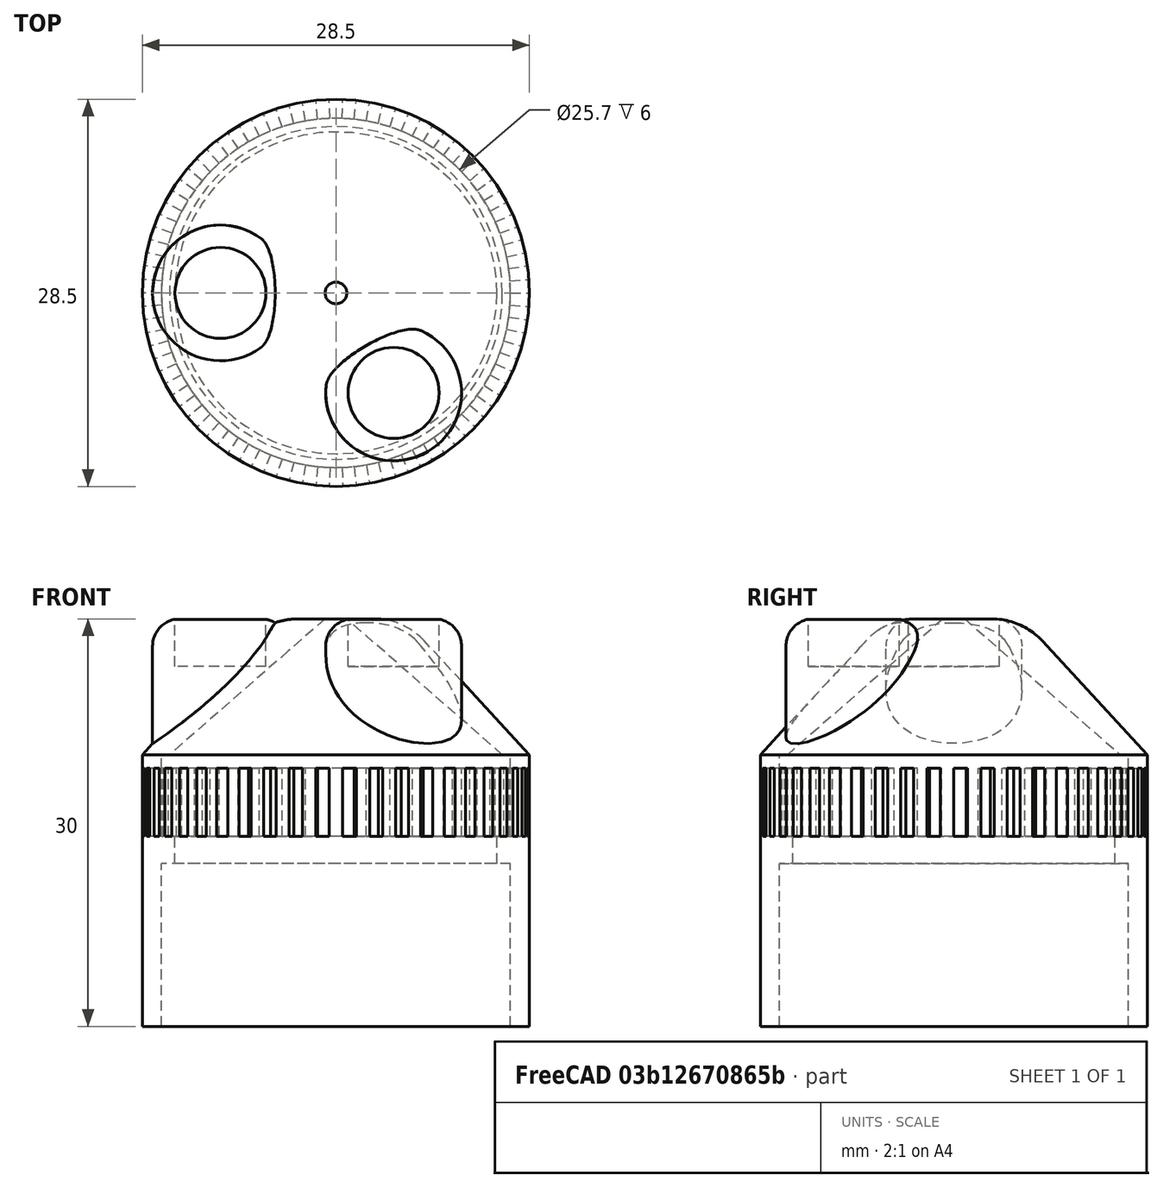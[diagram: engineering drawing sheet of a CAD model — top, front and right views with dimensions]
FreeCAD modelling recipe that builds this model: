
FCSTD DOCUMENT  (FreeCAD 0.17R11232 (Git))
Label: slotted_vial_to_funnel_adapter
License: All rights reserved
LicenseURL: http://en.wikipedia.org/wiki/All_rights_reserved
objects: Part::Feature×43, Part::Cylinder×9, Part::Cut×8, Part::MultiFuse×4, Part::Cone×3, Part::Fillet×3, Part::Box×1
note: 71 computed .brp shape members not serialized (recipe doc carries the construction recipe); baked Part::Feature solids carry a one-line shape summary decoded from their .brp

FEATURE [Part::Cylinder] Cylinder  label="outer_vial_sleeve_edge"
  Angle = 360
  AttacherType = Attacher::AttachEngine3D
  Height = 35
  Radius = 14.25
FEATURE [Part::Cylinder] Cylinder001  label="inner_vial_sleeve_edge"
  Angle = 360
  AttacherType = Attacher::AttachEngine3D
  Height = 35
  Radius = 12.85
FEATURE [Part::Cut] Cut  label="vial_sleeve"
  Base = -> Cylinder
  Tool = -> Cylinder001
FEATURE [Part::Cone] Cone  label="outer_ascent_cone_edge"
  Angle = 360
  AttacherType = Attacher::AttachEngine3D
  Height = 10
  Radius1 = 14.25
  Radius2 = 5
FEATURE [Part::Cone] Cone001  label="inner_ascent_cone_edge"
  Angle = 360
  AttacherType = Attacher::AttachEngine3D
  Height = 10
  Radius1 = 12.25
  Radius2 = 0.8
FEATURE [Part::Cut] Cut001  label="ascent_cone"
  Base = -> Cone
  Placement = pos=(0,0,35) rot=(0,0,1;0rad)
  Tool = -> Cone001
FEATURE [Part::Cylinder] Cylinder002  label="slot"
  Angle = 4
  AttacherType = Attacher::AttachEngine3D
  Height = 5
  Placement = pos=(0,0,29) rot=(0,0,1;0rad)
  Radius = 15
FEATURE [Part::Cylinder] Cylinder003  label="slot001"
  Angle = 4
  AttacherType = Attacher::AttachEngine3D
  Height = 5
  Placement = pos=(0,0,29) rot=(0,0,1;0.139626rad)
  Radius = 15
FEATURE [Part::Feature] Cylinder003002  label="slot003"
  Placement = pos=(0,0,29) rot=(0,0,1;0.279253rad)
  shape: bbox 14.42 x 5.13 x 5 mm, 5 faces (baked)
FEATURE [Part::Feature] slot_3  label="slot004"
  Placement = pos=(0,0,29) rot=(0,0,1;0.418879rad)
  shape: bbox 13.7 x 7.042 x 5 mm, 5 faces (baked)
FEATURE [Part::Feature] slot_4  label="slot005"
  Placement = pos=(0,0,29) rot=(0,0,1;0.558505rad)
  shape: bbox 12.72 x 8.817 x 5 mm, 5 faces (baked)
FEATURE [Part::Feature] slot_5  label="slot006"
  Placement = pos=(0,0,29) rot=(0,0,1;0.698132rad)
  shape: bbox 11.49 x 10.42 x 5 mm, 5 faces (baked)
FEATURE [Part::Feature] slot_6  label="slot007"
  Placement = pos=(0,0,29) rot=(0,0,1;0.837758rad)
  shape: bbox 10.04 x 11.82 x 5 mm, 5 faces (baked)
FEATURE [Part::Feature] slot_7  label="slot008"
  Placement = pos=(0,0,29) rot=(0,0,1;0.977384rad)
  shape: bbox 8.388 x 12.99 x 5 mm, 5 faces (baked)
FEATURE [Part::Feature] slot_8  label="slot009"
  Placement = pos=(0,0,29) rot=(0,0,1;1.11701rad)
  shape: bbox 6.576 x 13.91 x 5 mm, 5 faces (baked)
FEATURE [Part::Feature] slot_9  label="slot010"
  Placement = pos=(0,0,29) rot=(0,0,1;1.25664rad)
  shape: bbox 4.635 x 14.55 x 5 mm, 5 faces (baked)
FEATURE [Part::Feature] slot_10  label="slot011"
  Placement = pos=(0,0,29) rot=(0,0,1;1.39626rad)
  shape: bbox 2.605 x 14.92 x 5 mm, 5 faces (baked)
FEATURE [Part::Feature] slot_11  label="slot012"
  Placement = pos=(0,0,29) rot=(0,0,1;1.53589rad)
  shape: bbox 1.047 x 15 x 5 mm, 5 faces (baked)
FEATURE [Part::Feature] slot_12  label="slot013"
  Placement = pos=(0,0,29) rot=(0,0,1;1.67552rad)
  shape: bbox 2.605 x 14.92 x 5 mm, 5 faces (baked)
FEATURE [Part::Feature] slot_13  label="slot014"
  Placement = pos=(0,0,29) rot=(0,0,1;1.81514rad)
  shape: bbox 4.635 x 14.55 x 5 mm, 5 faces (baked)
FEATURE [Part::Feature] slot_14  label="slot015"
  Placement = pos=(0,0,29) rot=(0,0,1;1.95477rad)
  shape: bbox 6.576 x 13.91 x 5 mm, 5 faces (baked)
FEATURE [Part::Feature] slot_15  label="slot016"
  Placement = pos=(0,0,29) rot=(0,0,1;2.0944rad)
  shape: bbox 8.388 x 12.99 x 5 mm, 5 faces (baked)
FEATURE [Part::Feature] slot_16  label="slot017"
  Placement = pos=(0,0,29) rot=(0,0,1;2.23402rad)
  shape: bbox 10.04 x 11.82 x 5 mm, 5 faces (baked)
FEATURE [Part::Feature] slot_17  label="slot018"
  Placement = pos=(0,0,29) rot=(0,0,1;2.37365rad)
  shape: bbox 11.49 x 10.42 x 5 mm, 5 faces (baked)
FEATURE [Part::Feature] slot_18  label="slot019"
  Placement = pos=(0,0,29) rot=(0,0,1;2.51327rad)
  shape: bbox 12.72 x 8.817 x 5 mm, 5 faces (baked)
FEATURE [Part::Feature] slot_19  label="slot020"
  Placement = pos=(0,0,29) rot=(0,0,1;2.6529rad)
  shape: bbox 13.7 x 7.042 x 5 mm, 5 faces (baked)
FEATURE [Part::Feature] slot_20  label="slot021"
  Placement = pos=(0,0,29) rot=(0,0,1;2.79253rad)
  shape: bbox 14.42 x 5.13 x 5 mm, 5 faces (baked)
FEATURE [Part::Feature] slot_21  label="slot022"
  Placement = pos=(0,0,29) rot=(0,0,1;2.93215rad)
  shape: bbox 14.85 x 3.119 x 5 mm, 5 faces (baked)
FEATURE [Part::Feature] slot_22  label="slot023"
  Placement = pos=(0,0,29) rot=(0,0,1;3.07178rad)
  shape: bbox 15 x 1.046 x 5 mm, 5 faces (baked)
FEATURE [Part::Feature] slot_23  label="slot024"
  Placement = pos=(0,0,29) rot=(0,0,1;3.21141rad)
  shape: bbox 14.96 x 2.088 x 5 mm, 5 faces (baked)
FEATURE [Part::Feature] slot_24  label="slot025"
  Placement = pos=(0,0,29) rot=(0,0,1;3.35103rad)
  shape: bbox 14.67 x 4.135 x 5 mm, 5 faces (baked)
FEATURE [Part::Feature] slot_25  label="slot026"
  Placement = pos=(0,0,29) rot=(0,0,1;3.49066rad)
  shape: bbox 14.1 x 6.101 x 5 mm, 5 faces (baked)
FEATURE [Part::Feature] slot_26  label="slot027"
  Placement = pos=(0,0,29) rot=(0,0,1;3.63029rad)
  shape: bbox 13.24 x 7.949 x 5 mm, 5 faces (baked)
FEATURE [Part::Feature] slot_27  label="slot028"
  Placement = pos=(0,0,29) rot=(0,0,1;3.76991rad)
  shape: bbox 12.14 x 9.642 x 5 mm, 5 faces (baked)
FEATURE [Part::Feature] slot_28  label="slot029"
  Placement = pos=(0,0,29) rot=(0,0,1;3.90954rad)
  shape: bbox 10.79 x 11.15 x 5 mm, 5 faces (baked)
FEATURE [Part::Feature] slot_29  label="slot030"
  Placement = pos=(0,0,29) rot=(0,0,1;4.04916rad)
  shape: bbox 9.235 x 12.44 x 5 mm, 5 faces (baked)
FEATURE [Part::Feature] slot_30  label="slot031"
  Placement = pos=(0,0,29) rot=(0,0,1;4.18879rad)
  shape: bbox 7.5 x 13.48 x 5 mm, 5 faces (baked)
FEATURE [Part::Feature] slot_31  label="slot032"
  Placement = pos=(0,0,29) rot=(0,0,-1;1.95477rad)
  shape: bbox 5.619 x 14.27 x 5 mm, 5 faces (baked)
FEATURE [Part::Feature] slot_32  label="slot033"
  Placement = pos=(0,0,29) rot=(0,0,-1;1.81514rad)
  shape: bbox 3.629 x 14.77 x 5 mm, 5 faces (baked)
FEATURE [Part::Feature] slot_33  label="slot034"
  Placement = pos=(0,0,29) rot=(0,0,-1;1.67552rad)
  shape: bbox 1.568 x 14.99 x 5 mm, 5 faces (baked)
FEATURE [Part::Feature] slot_34  label="slot035"
  Placement = pos=(0,0,29) rot=(0,0,-1;1.53589rad)
  shape: bbox 1.568 x 14.99 x 5 mm, 5 faces (baked)
FEATURE [Part::Feature] slot_35  label="slot036"
  Placement = pos=(0,0,29) rot=(0,0,-1;1.39626rad)
  shape: bbox 3.629 x 14.77 x 5 mm, 5 faces (baked)
FEATURE [Part::Feature] slot_36  label="slot037"
  Placement = pos=(0,0,29) rot=(0,0,-1;1.25664rad)
  shape: bbox 5.619 x 14.27 x 5 mm, 5 faces (baked)
FEATURE [Part::Feature] slot_37  label="slot038"
  Placement = pos=(0,0,29) rot=(0,0,-1;1.11701rad)
  shape: bbox 7.5 x 13.48 x 5 mm, 5 faces (baked)
FEATURE [Part::Feature] slot_38  label="slot039"
  Placement = pos=(0,0,29) rot=(0,0,-1;0.977384rad)
  shape: bbox 9.235 x 12.44 x 5 mm, 5 faces (baked)
FEATURE [Part::Feature] slot_39  label="slot040"
  Placement = pos=(0,0,29) rot=(0,0,-1;0.837758rad)
  shape: bbox 10.79 x 11.15 x 5 mm, 5 faces (baked)
FEATURE [Part::Feature] slot_40  label="slot041"
  Placement = pos=(0,0,29) rot=(0,0,-1;0.698132rad)
  shape: bbox 12.14 x 9.642 x 5 mm, 5 faces (baked)
FEATURE [Part::Feature] slot_41  label="slot042"
  Placement = pos=(0,0,29) rot=(0,0,-1;0.558505rad)
  shape: bbox 13.24 x 7.949 x 5 mm, 5 faces (baked)
FEATURE [Part::Feature] slot_42  label="slot043"
  Placement = pos=(0,0,29) rot=(0,0,-1;0.418879rad)
  shape: bbox 14.1 x 6.101 x 5 mm, 5 faces (baked)
FEATURE [Part::Feature] slot_43  label="slot044"
  Placement = pos=(0,0,29) rot=(0,0,-1;0.279253rad)
  shape: bbox 14.67 x 4.135 x 5 mm, 5 faces (baked)
FEATURE [Part::Feature] slot_44  label="slot045"
  Placement = pos=(0,0,29) rot=(0,0,-1;0.139626rad)
  shape: bbox 14.96 x 2.088 x 5 mm, 5 faces (baked)
FEATURE [Part::MultiFuse] Fusion  label="slots"
  Shapes = -> [Cylinder002,Cylinder003002,slot_14,slot_15,slot_3,slot_11,slot_10,slot_7,slot_9,slot_4,slot_12,slot_13,Cylinder003,slot_16,slot_17,slot_18,slot_19,slot_6,slot_5,slot_8,slot_20,slot_21,slot_22,slot_23,slot_24,slot_25,slot_26,slot_27,slot_28,slot_29,slot_30,slot_31,slot_32,slot_33,slot_34,slot_35,slot_36,slot_37,slot_38,slot_39,slot_40,slot_41,slot_42,slot_43,slot_44]
FEATURE [Part::Cut] Cut002  label="slotted_vial_sleeve"
  Base = -> Cut
  Tool = -> Fusion
FEATURE [Part::Cylinder] Cylinder003003  label="lip_add"
  Angle = 360
  AttacherType = Attacher::AttachEngine3D
  Height = 2
  Placement = pos=(0,0,27) rot=(0,0,1;0rad)
  Radius = 12.85
FEATURE [Part::Cylinder] Cylinder003004  label="lip_subtract"
  Angle = 360
  AttacherType = Attacher::AttachEngine3D
  Height = 4
  Placement = pos=(0,0,26) rot=(0,0,1;0rad)
  Radius = 11.85
FEATURE [Part::Cut] Cut003  label="lip"
  Base = -> Cylinder003003
  Tool = -> Cylinder003004
FEATURE [Part::MultiFuse] Fusion001  label="slotted_lipped_vial_sleeve"
  Shapes = -> [Cut003,Cut002]
FEATURE [Part::Fillet] Fillet  label="rounded_ascent_cone"
  Base = -> Cut001
  Edges = 1 edges r=10: [Edge1]
FEATURE [Part::MultiFuse] Fusion002  label="too_tall_slotted_vial_to_funnel_adapter"
  Shapes = -> [Fillet,Fusion001]
FEATURE [Part::Box] Box  label="excess_sleeve_bottom"
  AttacherType = Attacher::AttachEngine3D
  Height = 15
  Length = 40
  Placement = pos=(-20,-20,0) rot=(0,0,1;0rad)
  Width = 40
FEATURE [Part::Cut] Cut004  label="slotted_vial_to_funnel_adapter"
  Base = -> Fusion002
  Placement = pos=(0,0,-15) rot=(0,0,1;0rad)
  Tool = -> Box
FEATURE [Part::Cylinder] Cylinder003005  label="magnet_pocket_1"
  Angle = 360
  AttacherType = Attacher::AttachEngine3D
  Height = 3.5
  Placement = pos=(-8.5,0,26.5) rot=(0,0,1;0rad)
  Radius = 3.35
FEATURE [Part::Cylinder] Cylinder003006  label="magnet_wall"
  Angle = 360
  AttacherType = Attacher::AttachEngine3D
  Height = 10
  Placement = pos=(-8.5,0,20) rot=(0,0,1;0rad)
  Radius = 5
FEATURE [Part::Cone] Cone002  label="inner_ascent_cone_copy"
  Angle = 360
  AttacherType = Attacher::AttachEngine3D
  Height = 10
  Placement = pos=(0,0,20) rot=(0,0,1;0rad)
  Radius1 = 12.25
  Radius2 = 0.8
FEATURE [Part::Cut] Cut005  label="mag_support_foundation"
  Base = -> Cylinder003006
  Tool = -> Cone002
FEATURE [Part::Fillet] Fillet001  label="smooth_mag_foundation_1"
  Base = -> Cut005
  Edges = 1 edges r=2: [Edge5]
FEATURE [Part::Fillet] Fillet002  label="smooth_mag_foundation_2"
  Base = -> Cut005
  Edges = 1 edges r=2: [Edge5]
  Placement = pos=(0,0,0) rot=(0,0,1;2.0944rad)
FEATURE [Part::Cylinder] Cylinder003007  label="magnet_pocket_2"
  Angle = 360
  AttacherType = Attacher::AttachEngine3D
  Height = 3.5
  Placement = pos=(4.25,-7.36122,26.5) rot=(0,0,1;2.0944rad)
  Radius = 3.35
FEATURE [Part::MultiFuse] Fusion003  label="slotted_funnel_w_magsupport"
  Shapes = -> [Fillet002,Fillet001,Cut004]
FEATURE [Part::Cut] Cut006
  Base = -> Fusion003
  Tool = -> Cylinder003007
FEATURE [Part::Cut] Cut007  label="slotted_vial_to_funnel_adapter_w_magnets"
  Base = -> Cut006
  Tool = -> Cylinder003005
